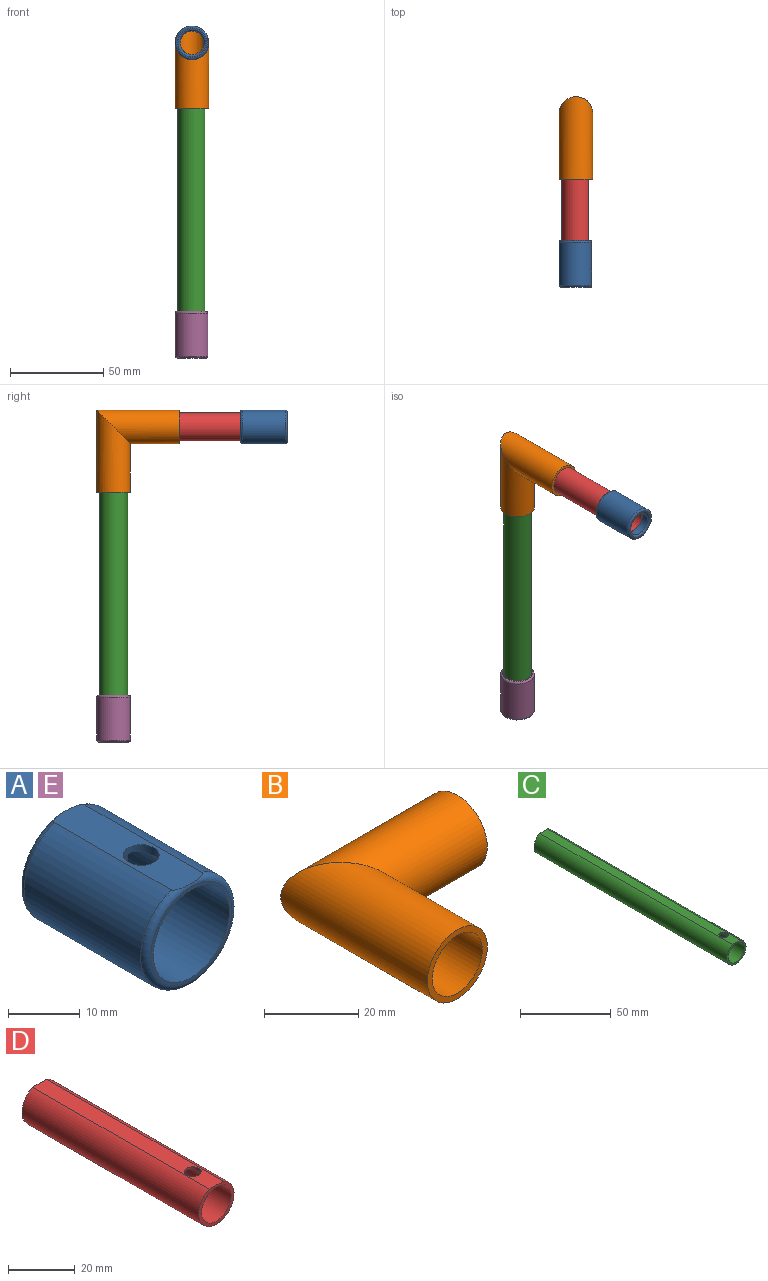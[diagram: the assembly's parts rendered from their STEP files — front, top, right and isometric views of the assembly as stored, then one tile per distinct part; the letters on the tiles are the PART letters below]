
ASSEMBLY  parts=5 mates=4
PART A: 11 faces, bbox 19.5x25x19.5 mm
  f0: cylinder r=6.5mm len=13mm, axis (0,1,0), area 163.4mm2, adj f5,f6
  f1: cylinder r=9mm len=23mm, axis (0,1,0), area 1159.9mm2, adj f7,f8,f9
  f2: plane 16x16mm, normal (0,-1,0), area 24.3mm2, adj f4,f8
  f3: plane 16x16mm, normal (0,1,0), area 24.3mm2, adj f6,f7
  f4: cylinder r=7.5mm len=20mm, axis (0,-1,0), area 922.5mm2, adj f2,f5,f10
  f5: plane 15x15mm, normal (0,-1,0), area 44mm2, adj f0,f4
  f6: torus R=7.5mm, axis (0,-1,0), area 67.7mm2, adj f0,f3
  f7: torus R=8mm, axis (0,-1,0), area 80.2mm2, adj f1,f3,f9
  f8: torus R=8mm, axis (0,-1,0), area 80.2mm2, adj f1,f2,f9
  f9: plane 24.75x6mm, normal (0,0,1), area 126.9mm2, adj f1,f7,f8,f10
  f10: cylinder r=2.5mm len=5mm, axis (0,0,1), area 18.8mm2, adj f4,f9
PART B: 6 faces, bbox 44x44x18 mm
  f0: cylinder r=7.5mm len=42.5mm, axis (1,0,0), area 1637.3mm2, adj f1,f2
  f1: cylinder r=7.5mm len=42.5mm, axis (0,1,0), area 1637.3mm2, adj f0,f3
  f2: plane 18x18mm, normal (1,0,0), area 77.8mm2, adj f0,f4
  f3: plane 18x18mm, normal (0,-1,0), area 77.8mm2, adj f1,f5
  f4: cylinder r=9mm len=44mm, axis (1,0,0), area 1961.8mm2, adj f2,f5
  f5: cylinder r=9mm len=44mm, axis (0,1,0), area 1961.8mm2, adj f3,f4
PART C: 6 faces, bbox 15x150x14.4 mm
  f0: cylinder r=6.28mm len=150mm, axis (0,1,0), area 5898.7mm2, adj f2,f3,f5
  f1: cylinder r=7.5mm len=150mm, axis (0,1,0), area 6162.5mm2, adj f2,f3,f4
  f2: plane 15x14.4mm, normal (0,-1,0), area 50.4mm2, adj f0,f1,f4
  f3: plane 15x14.4mm, normal (0,1,0), area 50.4mm2, adj f0,f1,f4
  f4: plane 150x5.88mm, normal (0,0,1), area 862.2mm2, adj f1,f2,f3,f5
  f5: cylinder r=2.5mm len=5mm, axis (0,0,1), area 13.8mm2, adj f0,f4
PART D: 6 faces, bbox 15x75x14.4 mm
  f0: cylinder r=6.28mm len=75mm, axis (0,1,0), area 2939.3mm2, adj f2,f3,f5
  f1: cylinder r=7.5mm len=75mm, axis (0,1,0), area 3081.2mm2, adj f2,f3,f4
  f2: plane 15x14.4mm, normal (0,-1,0), area 50.4mm2, adj f0,f1,f4
  f3: plane 15x14.4mm, normal (0,1,0), area 50.4mm2, adj f0,f1,f4
  f4: plane 75x5.88mm, normal (0,0,1), area 421.3mm2, adj f1,f2,f3,f5
  f5: cylinder r=2.5mm len=5mm, axis (0,0,1), area 13.8mm2, adj f0,f4
PART E: same geometry as A
PLACE A rot(axis=(0.71,0,0.71),180deg) t=(-99.98,-37.29,76.84)mm
PLACE B rot(axis=(0.58,-0.58,-0.58),120deg) t=(-99.98,-19.68,41.84)mm
PLACE C rot(axis=(0.58,0.58,0.58),120deg) t=(-99.98,55.57,63.22)mm
PLACE D rot(axis=(0,1,0),90deg) t=(-99.98,42.71,36)mm
PLACE E rot(axis=(-0.58,0.58,-0.58),120deg) t=(-99.98,55.57,-91.78)mm
MATE fastened B.f1 <-> C.f0  axis (0,0,1) through (-99.98,55.57,63.22)mm
MATE fastened A.f0 <-> D.f0  axis (0,1,0) through (-99.98,-32.29,76.84)mm
MATE fastened B.f4 <-> D.f0  axis (0,-1,0) through (-99.98,42.71,76.84)mm
MATE fastened E.f4 <-> C.f1  axis (0,0,1) through (-99.98,55.57,-86.78)mm
